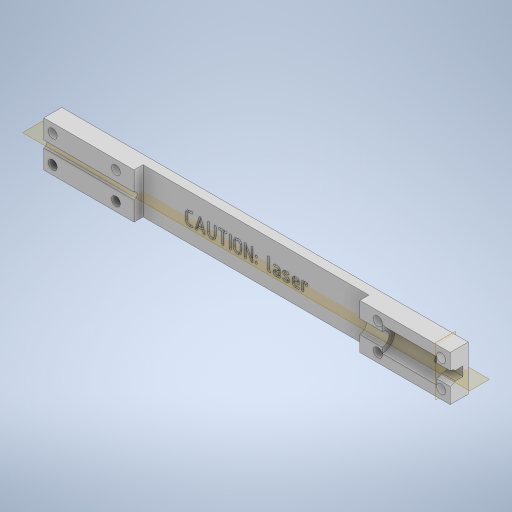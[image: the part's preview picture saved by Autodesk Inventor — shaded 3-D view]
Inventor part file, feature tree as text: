
AUTODESK INVENTOR PART (.ipt)
format: ipt  version: 2024 (Build 280153000, 153)  size: 574,464 bytes
history: native  units: mm
features: extrude x8, sketch x8, plane x2
ambient origin geometry x8: Origin, YZ Plane, XZ Plane, XY Plane, X Axis, Y Axis, Z Axis, Center Point
bodies: Solid1 (feature_tree)
feature tree (18):
  extrude  "Extrusion1"  Depth=10.0mm
  extrude  "Extrusion4"  Depth=20.0mm
  extrude  "Extrusion5"  Depth=2.0mm TaperAngle=0.0deg
  extrude  "Extrusion6"  Depth=2.0mm
  extrude  "Extrusion7"  Depth=2.0mm
  plane  "Work Plane1"
  extrude  "Extrusion8"  Depth=2.0mm
  plane  "Work Plane3"
  extrude  "Extrusion10"  Depth=2.0mm
  extrude  "Extrusion11"  Depth=3.0mm
  sketch  "Sketch1"  dims[d0=90.0mm d1=10.0mm]
  sketch  "Sketch4"  dims[d2=2.0mm d3=0.0mm d13=20.0mm]
  sketch  "Sketch5"  dims[d14=20.0mm d15=2.0mm d16=0.0mm]
  sketch  "Sketch6"  dims[d17=2.0mm d18=2.0mm]
  sketch  "Sketch7"  dims[d19=2.0mm d20=2.0mm]
  sketch  "Sketch8"  dims[d22=2.0mm d23=2.0mm]
  sketch  "Sketch10"  dims[d24=2.0mm d25=2.0mm]
  sketch  "Sketch11"  dims[d26=0.0mm d27=0.0mm d28=3.0mm d29=20.0mm d30=0.0mm d31=1.5mm d32=20.0mm d33=0.0mm d34=-3.0mm d35=5.4mm d36=12.0mm d37=0.0mm d38=-5.0mm d42=6.0mm d43=2.8mm d44=2.0mm d45=0.0mm d46=0.5mm d47=0.0mm d4=0.5mm d5=0.872665mm d6=0.5mm d7=0.872665mm]
